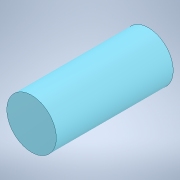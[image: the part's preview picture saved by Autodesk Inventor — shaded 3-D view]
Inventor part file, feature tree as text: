
AUTODESK INVENTOR PART (.ipt)
format: ipt  version: 2022 (Build 260153000, 153)  size: 100,352 bytes
history: native  units: in
note: dims shown in document units (in); Inventor stores cm internally (conversion verified against a paired STEP export)
features: extrude x1, sketch x1
ambient origin geometry x8: Origin, YZ Plane, XZ Plane, XY Plane, X Axis, Y Axis, Z Axis, Center Point
bodies: Solid1 (feature_tree)
feature tree (2):
  extrude  "Extrusion1"  Depth=0.5906in
  sketch  "Sketch2"  dims[d0=0.5906in d1=0.0in d2=0.0197in d3=0.0344in d4=0.0197in d5=0.0344in]
